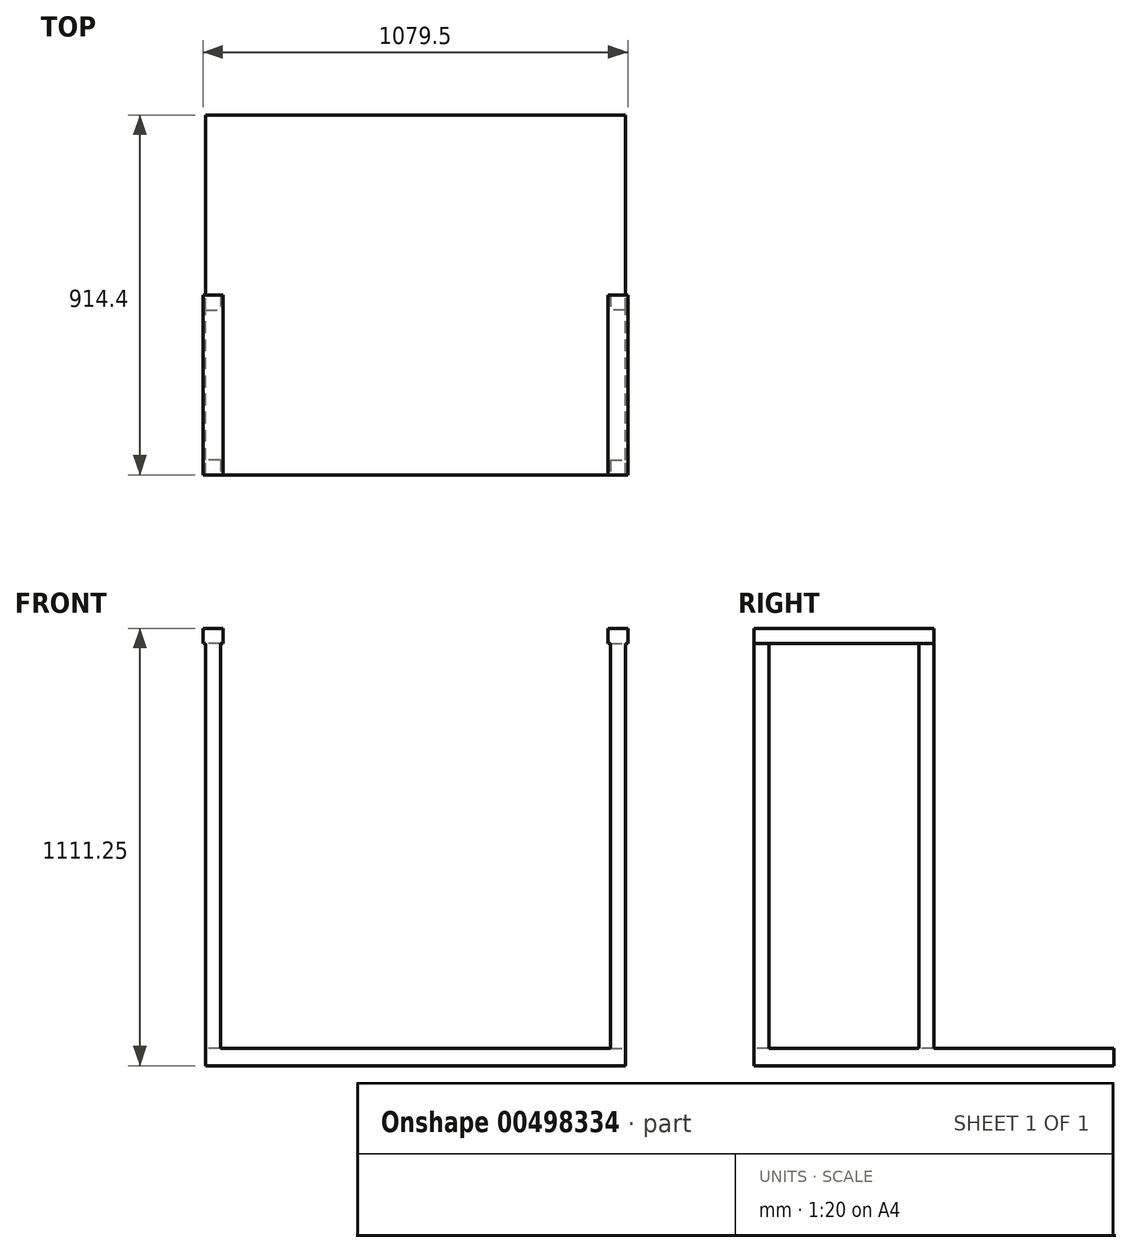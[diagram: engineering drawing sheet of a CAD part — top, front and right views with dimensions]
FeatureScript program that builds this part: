
annotation { "Feature Type Name" : "Feature", "Feature Type Description" : "" }
export const myFeature = defineFeature(function(context is Context, id is Id, definition is map)
    precondition{}
    {
        {
            var Q0;
            Q0=qCreatedBy(makeId("Top.planeOp"),FACE);
            var sketch = newSketch(context, id + "F0", { "sketchPlane" : qUnion([Q0])});
            skLineSegment(sketch, "E0.bottom", {"start": v(-533.4, 457.2) * mm, "end": v(533.4, 457.2) * mm});
            skLineSegment(sketch, "E0.top", {"start": v(-533.4, -457.2) * mm, "end": v(533.4, -457.2) * mm});
            skLineSegment(sketch, "E0.left", {"start": v(-533.4, 457.2) * mm, "end": v(-533.4, -457.2) * mm});
            skLineSegment(sketch, "E0.right", {"start": v(533.4, 457.2) * mm, "end": v(533.4, -457.2) * mm});
            skPoint(sketch, "E0.middle", {"position": v(0, 0) * mm});
            skLineSegment(sketch, "E1", {"start": v(0, 457.2) * mm, "end": v(0, -457.2) * mm});
            skLineSegment(sketch, "E2", {"start": v(-533.4, 0) * mm, "end": v(533.4, 0) * mm});
            skSolve(sketch);
        }
        {
            var Q0;
            Q0 = qSketchRegion(id + "F0", true);
            extrude(context, id + "F1", {"entities" : qUnion([Q0]), "depth" : 44.45 * mm});
        }
        {
            var Q0;
            Q0=makeQuery(id+"F1.opExtrude","CAP_FACE",FACE,{"disambiguationData":[OSD([sQuery(id+"F0.wireOp",EDGE,"E0.bottom"),sQuery(id+"F0.wireOp",EDGE,"E0.top"),sQuery(id+"F0.wireOp",EDGE,"E0.left"),sQuery(id+"F0.wireOp",EDGE,"E0.right")])],"isStart":false});
            var sketch = newSketch(context, id + "F2", { "sketchPlane" : qUnion([Q0])});
            skLineSegment(sketch, "E3.bottom", {"start": v(-495.3, 419.1) * mm, "end": v(-533.4, 419.1) * mm});
            skLineSegment(sketch, "E3.top", {"start": v(-495.3, 457.2) * mm, "end": v(-533.4, 457.2) * mm});
            skLineSegment(sketch, "E3.left", {"start": v(-495.3, 419.1) * mm, "end": v(-495.3, 457.2) * mm});
            skLineSegment(sketch, "E3.right", {"start": v(-533.4, 419.1) * mm, "end": v(-533.4, 457.2) * mm});
            skPoint(sketch, "E3.middle", {"position": v(-514.35, 438.15) * mm});
            skLineSegment(sketch, "E4.MirrorCS", {"start": v(533.4, 419.1) * mm, "end": v(533.4, 457.2) * mm});
            skLineSegment(sketch, "E5.MirrorCS", {"start": v(495.3, 419.1) * mm, "end": v(533.4, 419.1) * mm});
            skLineSegment(sketch, "E6.MirrorCS", {"start": v(495.3, 457.2) * mm, "end": v(533.4, 457.2) * mm});
            skLineSegment(sketch, "E7.MirrorCS", {"start": v(495.3, 419.1) * mm, "end": v(495.3, 457.2) * mm});
            skPoint(sketch, "E8.MirrorP", {"position": v(514.35, 438.15) * mm});
            skLineSegment(sketch, "E9.bottom", {"start": v(-533.4, 0) * mm, "end": v(-495.3, 0) * mm});
            skLineSegment(sketch, "E9.top", {"start": v(-533.4, 38.1) * mm, "end": v(-495.3, 38.1) * mm});
            skLineSegment(sketch, "E9.left", {"start": v(-533.4, 0) * mm, "end": v(-533.4, 38.1) * mm});
            skLineSegment(sketch, "E9.right", {"start": v(-495.3, 0) * mm, "end": v(-495.3, 38.1) * mm});
            skLineSegment(sketch, "E10.MirrorCS", {"start": v(533.4, 38.1) * mm, "end": v(495.3, 38.1) * mm});
            skLineSegment(sketch, "E11.MirrorCS", {"start": v(533.4, 0) * mm, "end": v(495.3, 0) * mm});
            skLineSegment(sketch, "E12.MirrorCS", {"start": v(495.3, 0) * mm, "end": v(495.3, 38.1) * mm});
            skLineSegment(sketch, "E13.MirrorCS", {"start": v(533.4, 0) * mm, "end": v(533.4, 38.1) * mm});
            skSolve(sketch);
        }
        {
            var Q0;
            Q0 = qSketchRegion(id + "F2", true);
            extrude(context, id + "F3", {"entities" : qUnion([Q0]), "operationType" : NewBodyOperationType.ADD, "depth" : 1066.8 * mm});
        }
        {
            var Q0;
            Q0=makeQuery(id+"F3.opExtrude","CAP_FACE",FACE,{"disambiguationData":[OSD([sQuery(id+"F2.wireOp",EDGE,"E3.bottom"),sQuery(id+"F2.wireOp",EDGE,"E3.top"),sQuery(id+"F2.wireOp",EDGE,"E3.left"),sQuery(id+"F2.wireOp",EDGE,"E3.right")])],"isStart":false});
            var sketch = newSketch(context, id + "F4", { "sketchPlane" : qUnion([Q0])});
            skLineSegment(sketch, "E14.bottom", {"start": v(-488.95, 457.2) * mm, "end": v(-539.75, 457.2) * mm});
            skLineSegment(sketch, "E14.top", {"start": v(-488.95, 0) * mm, "end": v(-539.75, 0) * mm});
            skLineSegment(sketch, "E14.left", {"start": v(-488.95, 457.2) * mm, "end": v(-488.95, 0) * mm});
            skLineSegment(sketch, "E14.right", {"start": v(-539.75, 457.2) * mm, "end": v(-539.75, 0) * mm});
            skPoint(sketch, "E14.middle", {"position": v(-514.35, 228.6) * mm});
            skPoint(sketch, "E14.middle.positionSnap0", {"position": v(-514.35, 419.1) * mm});
            skPoint(sketch, "E14.centerSnap0", {"position": v(-514.35, 419.1) * mm});
            skLineSegment(sketch, "E15.MirrorCS", {"start": v(488.95, 457.2) * mm, "end": v(539.75, 457.2) * mm});
            skLineSegment(sketch, "E16.MirrorCS", {"start": v(488.95, 0) * mm, "end": v(539.75, 0) * mm});
            skLineSegment(sketch, "E17.MirrorCS", {"start": v(539.75, 457.2) * mm, "end": v(539.75, 0) * mm});
            skLineSegment(sketch, "E18.MirrorCS", {"start": v(488.95, 457.2) * mm, "end": v(488.95, 0) * mm});
            skSolve(sketch);
        }
        {
            var Q0;
            Q0 = qSketchRegion(id + "F4", true);
            extrude(context, id + "F5", {"entities" : qUnion([Q0]), "operationType" : NewBodyOperationType.ADD, "oppositeDirection" : true, "depth" : 38.1 * mm});
        }
        {
            var Q0;
            Q0=makeQuery(id+"F1.opExtrude","SWEPT_BODY",BODY,{"disambiguationData":[OSD([sQuery(id+"F0.wireOp",EDGE,"E0.bottom"),sQuery(id+"F0.wireOp",EDGE,"E0.top"),sQuery(id+"F0.wireOp",EDGE,"E0.left"),sQuery(id+"F0.wireOp",EDGE,"E0.right")])]});
            var Q1;
            Q1=makeQuery(id+"F1.opExtrude","SWEPT_EDGE",EDGE,{"disambiguationData":[OSD([sQuery(id+"F0.wireOp",EDGE,"E0.top"),sQuery(id+"F0.wireOp",EDGE,"E0.left")])]});
            transform(context, id + "F6", {"entities" : qUnion([Q0]), "transformType" : TransformType.ROTATION, "transformAxis" : qUnion([Q1]), "angle" : 180 * degree, "makeCopy" : false});
        }
        {
            var Q0;
            Q0=makeQuery(id+"F1.opExtrude","SWEPT_BODY",BODY,{"disambiguationData":[OSD([sQuery(id+"F0.wireOp",EDGE,"E0.bottom"),sQuery(id+"F0.wireOp",EDGE,"E0.top"),sQuery(id+"F0.wireOp",EDGE,"E0.left"),sQuery(id+"F0.wireOp",EDGE,"E0.right")])]});
            transform(context, id + "F7", {"entities" : qUnion([Q0]), "transformType" : TransformType.TRANSLATION_3D, "dx" : 1155.7 * mm, "dy" : 833.12 * mm, "dz" : 0 * mm, "makeCopy" : false});
        }
    });
